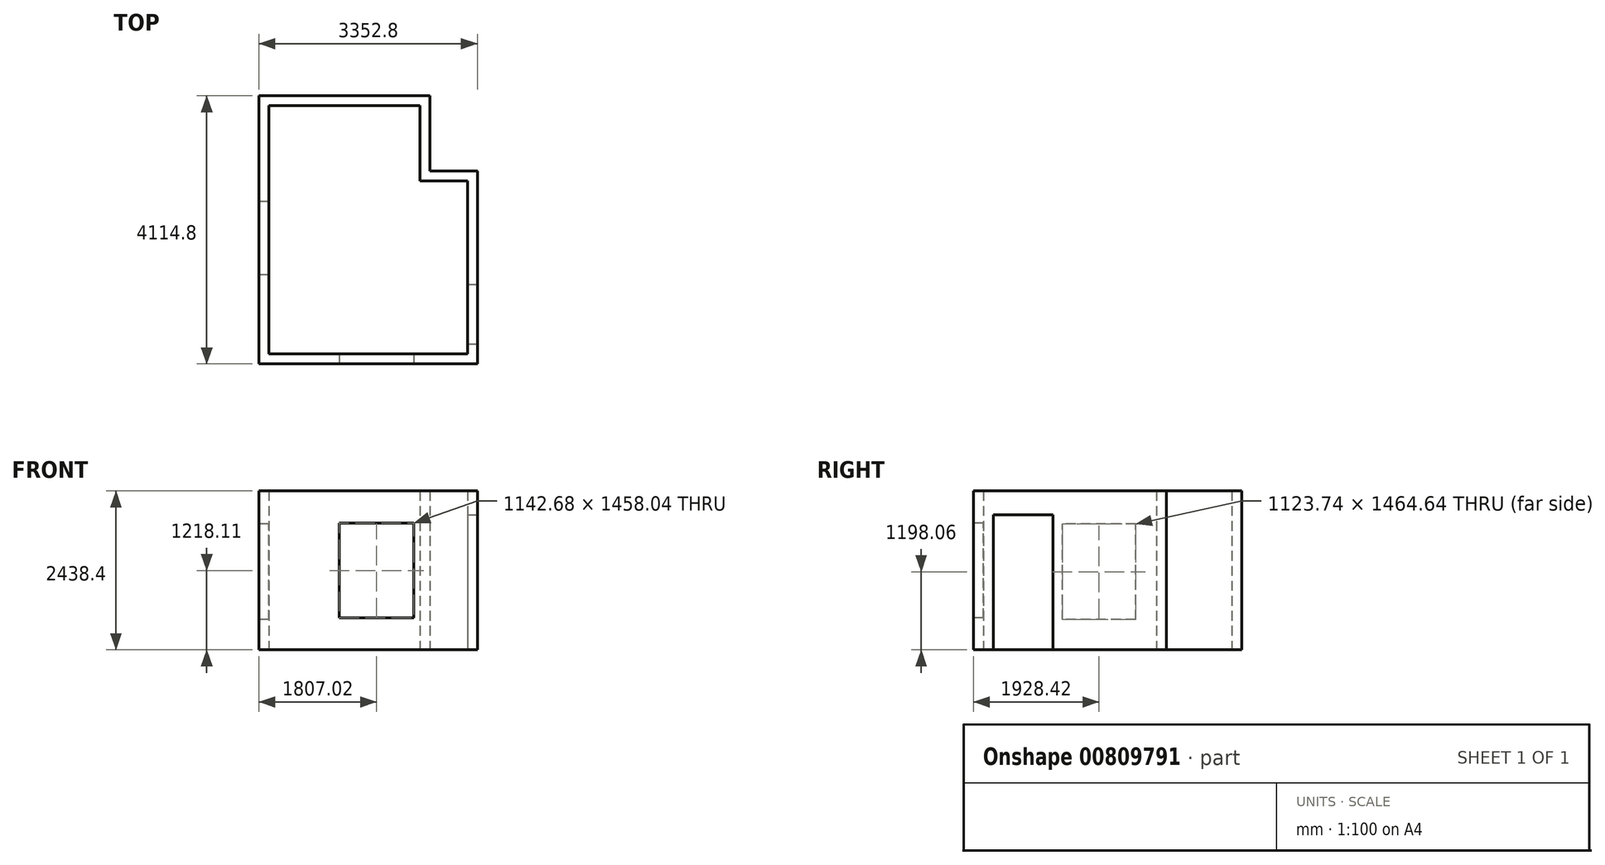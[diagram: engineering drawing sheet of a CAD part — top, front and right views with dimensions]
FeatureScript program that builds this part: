
annotation { "Feature Type Name" : "Feature", "Feature Type Description" : "" }
export const myFeature = defineFeature(function(context is Context, id is Id, definition is map)
    precondition{}
    {
        {
            var Q0;
            Q0=qCreatedBy(makeId("Top.planeOp"),FACE);
            var sketch = newSketch(context, id + "F0", { "sketchPlane" : qUnion([Q0])});
            skLineSegment(sketch, "E0", {"start": v(0, 0) * mm, "end": v(0, 3810) * mm});
            skLineSegment(sketch, "E1", {"start": v(0, 3810) * mm, "end": v(2317.75, 3810) * mm});
            skLineSegment(sketch, "E2", {"start": v(3048, 2654.3) * mm, "end": v(3048, 0) * mm});
            skLineSegment(sketch, "E3", {"start": v(2317.75, 3810) * mm, "end": v(2317.75, 2654.3) * mm});
            skLineSegment(sketch, "E4", {"start": v(2317.75, 2654.3) * mm, "end": v(3048, 2654.3) * mm});
            skLineSegment(sketch, "E5", {"start": v(3048, 0) * mm, "end": v(0, 0) * mm});
            skLineSegment(sketch, "E6.0", {"start": v(-152.4, -152.4) * mm, "end": v(-152.4, 3962.4) * mm});
            skLineSegment(sketch, "E6.1", {"start": v(2470.15, 3962.4) * mm, "end": v(2470.15, 2806.7) * mm});
            skLineSegment(sketch, "E6.2", {"start": v(2470.15, 2806.7) * mm, "end": v(3200.4, 2806.7) * mm});
            skLineSegment(sketch, "E6.3", {"start": v(-152.4, 3962.4) * mm, "end": v(2470.15, 3962.4) * mm});
            skLineSegment(sketch, "E6.4", {"start": v(3200.4, 2806.7) * mm, "end": v(3200.4, -152.4) * mm});
            skLineSegment(sketch, "E6.5", {"start": v(3200.4, -152.4) * mm, "end": v(-152.4, -152.4) * mm});
            skSolve(sketch);
        }
        {
            var Q0;
            Q0 = qSketchRegion(id + "F0", true);
            extrude(context, id + "F1", {"entities" : qUnion([Q0]), "depth" : 2438.4 * mm, "offsetDistance" : 25.4 * mm});
        }
        {
            var Q0;
            Q0=makeQuery(id+"F1.opExtrude","SWEPT_FACE",FACE,{"disambiguationData":[OSD([sQuery(id+"F0.wireOp",EDGE,"E6.4")])]});
            var sketch = newSketch(context, id + "F2", { "sketchPlane" : qUnion([Q0])});
            skLineSegment(sketch, "E7.bottom", {"start": v(152.4, 0) * mm, "end": v(1066.8, 0) * mm});
            skLineSegment(sketch, "E7.top", {"start": v(152.4, 2070.1) * mm, "end": v(1066.8, 2070.1) * mm});
            skLineSegment(sketch, "E7.left", {"start": v(152.4, 0) * mm, "end": v(152.4, 2070.1) * mm});
            skLineSegment(sketch, "E7.right", {"start": v(1066.8, 0) * mm, "end": v(1066.8, 2070.1) * mm});
            skSolve(sketch);
        }
        {
            var Q0;
            Q0 = qSketchRegion(id + "F2", true);
            extrude(context, id + "F3", {"entities" : qUnion([Q0]), "operationType" : NewBodyOperationType.REMOVE, "endBound" : BoundingType.UP_TO_NEXT, "oppositeDirection" : true, "depth" : 25.4 * mm, "offsetDistance" : 25.4 * mm});
        }
        {
            var Q0;
            Q0=makeQuery(id+"F1.opExtrude","SWEPT_FACE",FACE,{"disambiguationData":[OSD([sQuery(id+"F0.wireOp",EDGE,"E6.5")])]});
            var sketch = newSketch(context, id + "F4", { "sketchPlane" : qUnion([Q0])});
            skLineSegment(sketch, "E8.bottom", {"start": v(1083.28, 1947.13) * mm, "end": v(2225.96, 1947.13) * mm});
            skLineSegment(sketch, "E8.top", {"start": v(1083.28, 489.1) * mm, "end": v(2225.96, 489.1) * mm});
            skLineSegment(sketch, "E8.left", {"start": v(1083.28, 1947.13) * mm, "end": v(1083.28, 489.1) * mm});
            skLineSegment(sketch, "E8.right", {"start": v(2225.96, 1947.13) * mm, "end": v(2225.96, 489.1) * mm});
            skSolve(sketch);
        }
        {
            var Q0;
            Q0 = qSketchRegion(id + "F4", true);
            extrude(context, id + "F5", {"entities" : qUnion([Q0]), "operationType" : NewBodyOperationType.REMOVE, "endBound" : BoundingType.UP_TO_NEXT, "oppositeDirection" : true, "depth" : 25.4 * mm, "offsetDistance" : 25.4 * mm});
        }
        {
            var Q0;
            Q0=makeQuery(id+"F1.opExtrude","SWEPT_FACE",FACE,{"disambiguationData":[OSD([sQuery(id+"F0.wireOp",EDGE,"E6.0")])]});
            var sketch = newSketch(context, id + "F6", { "sketchPlane" : qUnion([Q0])});
            skLineSegment(sketch, "E9.bottom", {"start": v(-1214.15, 1930.38) * mm, "end": v(-2337.9, 1930.38) * mm});
            skLineSegment(sketch, "E9.top", {"start": v(-1214.15, 465.74) * mm, "end": v(-2337.9, 465.74) * mm});
            skLineSegment(sketch, "E9.left", {"start": v(-1214.15, 1930.38) * mm, "end": v(-1214.15, 465.74) * mm});
            skLineSegment(sketch, "E9.right", {"start": v(-2337.9, 1930.38) * mm, "end": v(-2337.9, 465.74) * mm});
            skSolve(sketch);
        }
        {
            var Q0;
            Q0 = qSketchRegion(id + "F6", true);
            extrude(context, id + "F7", {"entities" : qUnion([Q0]), "operationType" : NewBodyOperationType.REMOVE, "endBound" : BoundingType.UP_TO_NEXT, "oppositeDirection" : true, "depth" : 25.4 * mm, "offsetDistance" : 25.4 * mm});
        }
    });
